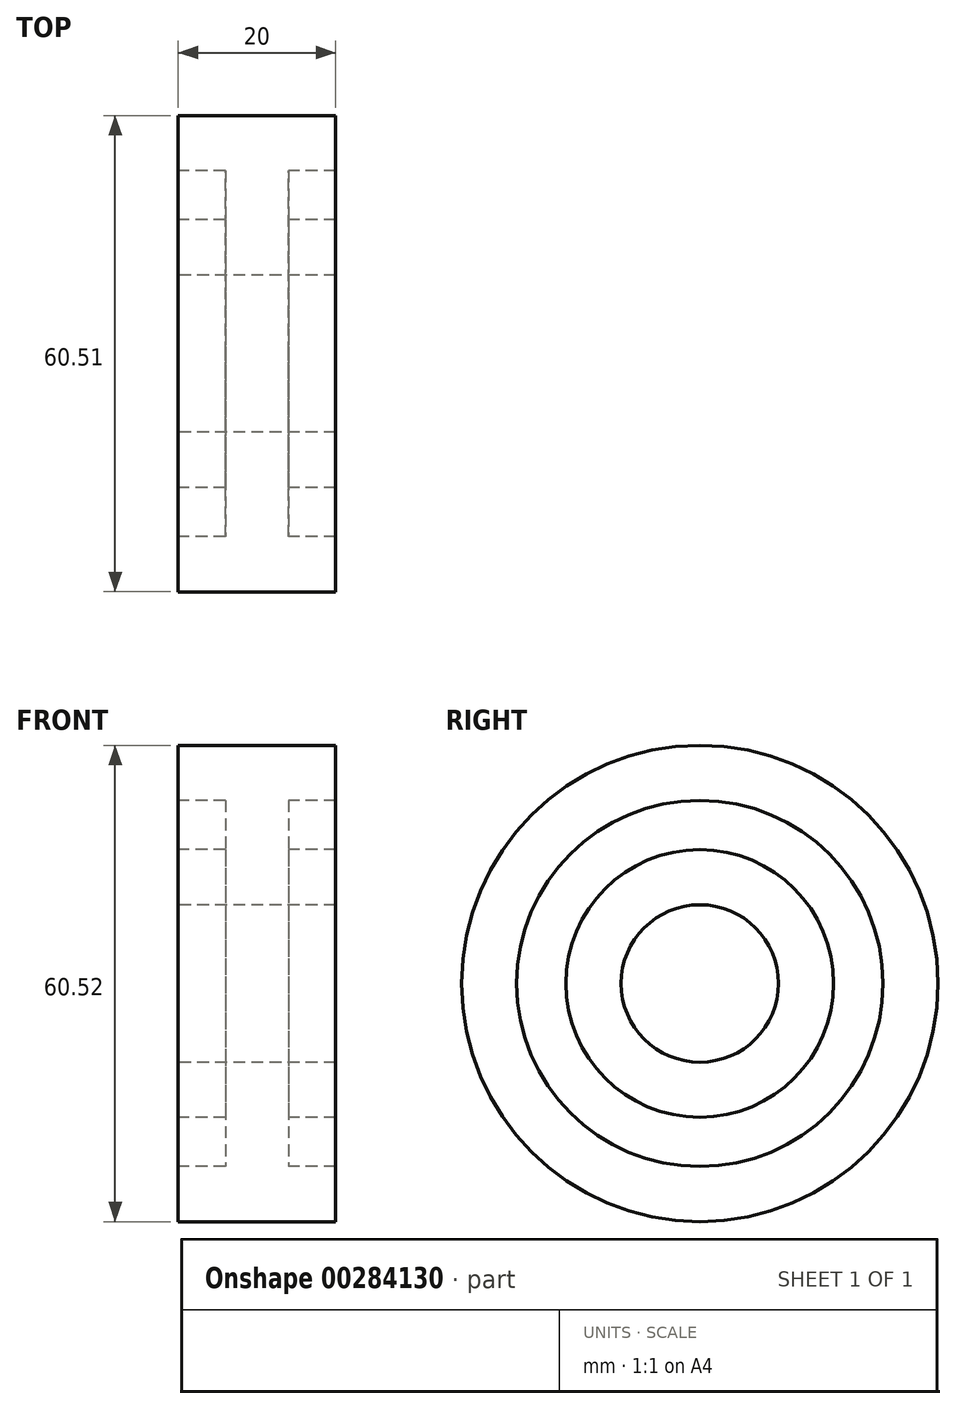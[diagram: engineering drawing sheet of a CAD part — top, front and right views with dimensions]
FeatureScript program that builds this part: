
annotation { "Feature Type Name" : "Feature", "Feature Type Description" : "" }
export const myFeature = defineFeature(function(context is Context, id is Id, definition is map)
    precondition{}
    {
        {
            var Q0;
            Q0=qCreatedBy(makeId("Top.planeOp"),FACE);
            var sketch = newSketch(context, id + "F0", { "sketchPlane" : qUnion([Q0])});
            skLineSegment(sketch, "E0.bottom", {"start": v(-49.03, 54.52) * mm, "end": v(-29.03, 54.52) * mm});
            skLineSegment(sketch, "E0.top", {"start": v(-49.03, 47.52) * mm, "end": v(-43.03, 47.52) * mm});
            skLineSegment(sketch, "E0.left", {"start": v(-49.03, 54.52) * mm, "end": v(-49.03, 47.52) * mm});
            skLineSegment(sketch, "E0.right", {"start": v(-29.03, 54.52) * mm, "end": v(-29.03, 47.52) * mm});
            skLineSegment(sketch, "E1.bottom", {"start": v(-49.03, 41.26) * mm, "end": v(-43.03, 41.26) * mm});
            skLineSegment(sketch, "E1.top", {"start": v(-49.03, 34.26) * mm, "end": v(-29.03, 34.26) * mm});
            skLineSegment(sketch, "E1.left", {"start": v(-49.03, 41.26) * mm, "end": v(-49.03, 34.26) * mm});
            skLineSegment(sketch, "E1.right", {"start": v(-29.03, 41.26) * mm, "end": v(-29.03, 34.26) * mm});
            skLineSegment(sketch, "E2", {"start": v(-43.03, 47.52) * mm, "end": v(-43.03, 41.26) * mm});
            skLineSegment(sketch, "E3", {"start": v(-35.03, 47.52) * mm, "end": v(-35.03, 41.26) * mm});
            skLineSegment(sketch, "E4.trimOffspring", {"start": v(-35.03, 41.26) * mm, "end": v(-29.03, 41.26) * mm});
            skLineSegment(sketch, "E5.trimOffspring", {"start": v(-35.03, 47.52) * mm, "end": v(-29.03, 47.52) * mm});
            skLineSegment(sketch, "E6", {"start": v(-75.97, 24.26) * mm, "end": v(9.4, 24.26) * mm, "construction": true});
            skSolve(sketch);
        }
        {
            var Q0;
            Q0=makeQuery(id+"F0.imprint","IMPRINT",FACE,{"disambiguationData":[TD([[makeQuery(id+"F0.imprint","IMPRINT",EDGE,{"derivedFrom":sQuery(id+"F0.wireOp",EDGE,"E0.bottom")}),-1.0]])]});
            var Q1;
            Q1=sQuery(id+"F0.wireOp",EDGE,"E6");
            revolve(context, id + "F1", {"entities" : qUnion([Q0]), "axis" : qUnion([Q1]), "revolveType" : RevolveType.FULL});
        }
    });
